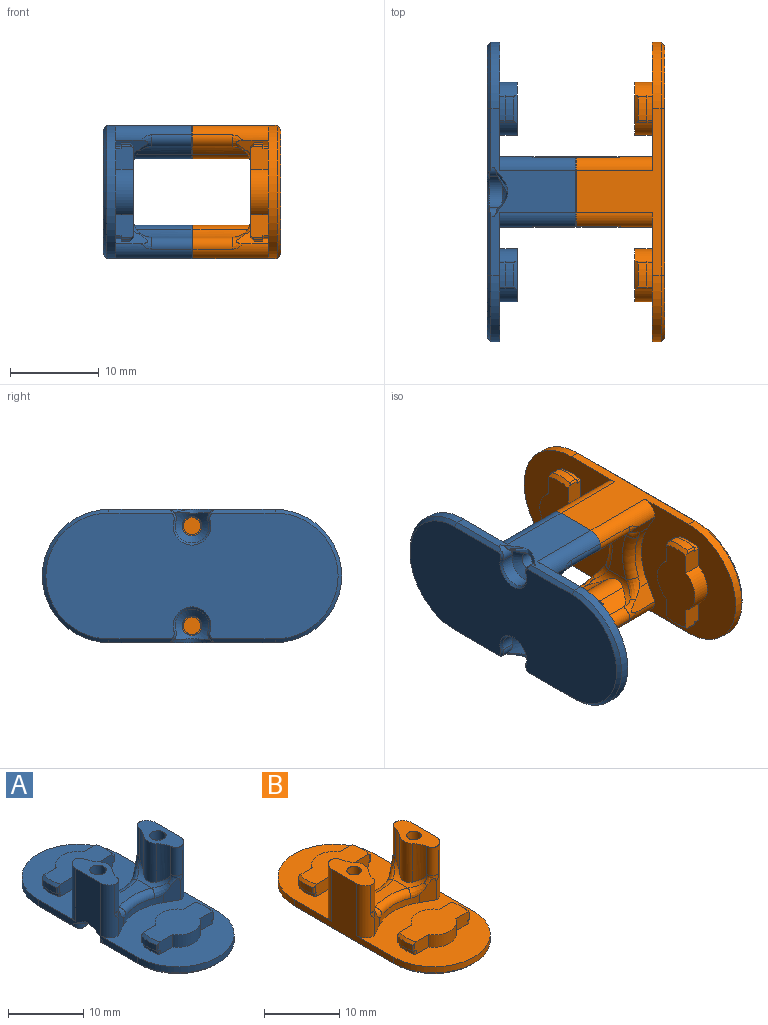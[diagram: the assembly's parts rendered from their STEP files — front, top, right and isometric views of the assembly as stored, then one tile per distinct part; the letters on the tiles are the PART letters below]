
ASSEMBLY  parts=2 mates=1
PART A: 116 faces, bbox 16.5x33.9x10.1 mm
  f0: plane 2.76x2mm, normal (0,-1,0), area 5mm2, adj f2,f13,f71,f76,f99,f105,f114
  f1: plane 2.57x2mm, normal (0,1,0), area 5mm2, adj f12,f78,f83,f87,f93,f101,f109
  f2: cylinder r=5.55mm len=2.91mm, axis (0,0,-1), area 2.9mm2, adj f0,f84,f99,f114,f115
  f3: cylinder r=5.55mm len=2.72mm, axis (0,0,-1), area 2.8mm2, adj f86,f95,f110,f111
  f4: cylinder r=7.55mm len=7.55mm, axis (0,0,1), area 8.2mm2, adj f11,f12,f38,f39,f88,f89
  f5: cylinder r=7.55mm len=7.55mm, axis (0,0,1), area 8.2mm2, adj f9,f13,f33,f34,f90,f91
  f6: cylinder r=1.6mm len=8.6mm, axis (0,0,1), area 19mm2, adj f10,f12,f26,f28,f37,f89
  f7: cylinder r=1.6mm len=8.6mm, axis (0,0,1), area 19mm2, adj f8,f13,f23,f24,f32,f91
  f8: bspline ~2.21x1.97mm, area 1.8mm2, adj f7,f9,f21,f32,f91
  f9: bspline ~2.95x2.65mm, area 2.9mm2, adj f5,f8,f21,f33,f91
  f10: bspline ~2.21x1.97mm, area 1.8mm2, adj f6,f11,f22,f37,f89
  f11: bspline ~2.95x2.65mm, area 2.9mm2, adj f4,f10,f22,f38,f89
  f12: plane 15.05x15mm, normal (0,0,1), area 143.6mm2, adj f1,f4,f6,f24,f26,f27,f30,f78
  f13: plane 15.05x15mm, normal (0,0,1), area 143.6mm2, adj f0,f5,f7,f24,f25,f26,f31,f70
  f14: plane 0.09x0mm, normal (0,0,-1), area 0mm2, adj f24,f59
  f15: plane 0.09x0mm, normal (0,0,-1), area 0mm2, adj f26,f57
  f16: plane 32.95x14.2mm, normal (0,0,-1), area 397.9mm2, adj f19,f20,f48,f49,f50,f51,f62,f63
  f17: cylinder r=1.1mm len=7.5mm, axis (0,0,1), area 51.8mm2, adj f23,f61
  f18: cylinder r=1.1mm len=7.5mm, axis (0,0,1), area 51.8mm2, adj f28,f60
  f19: plane 7.23x0.48mm, normal (0.71,0,-0.71), area 4mm2, adj f16,f24,f51,f58,f65
  f20: plane 7.23x0.48mm, normal (-0.71,0,-0.71), area 4mm2, adj f16,f26,f48,f57,f62
  f21: cylinder r=2mm len=5.89mm, axis (0,1,0), area 6.2mm2, adj f8,f9,f29,f39,f40,f42,f43,f44
  f22: cylinder r=2mm len=5.89mm, axis (0,-1,0), area 6.2mm2, adj f10,f11,f29,f34,f35,f45,f46,f47
  f23: plane 7.89x3.75mm, normal (0,0,1), area 18mm2, adj f7,f17,f24,f30,f32,f41,f42,f43
  f24: plane 18.89x9.74mm, normal (1,0,0), area 52.5mm2, adj f7,f12,f13,f14,f19,f23,f25,f27
  f25: cylinder r=7.5mm len=15mm, axis (0,0,-1), area 23.6mm2, adj f13,f24,f26,f51
  f26: plane 18.89x9.74mm, normal (-1,0,0), area 52.5mm2, adj f6,f12,f13,f15,f20,f25,f27,f28
  f27: cylinder r=7.5mm len=15mm, axis (0,0,-1), area 23.6mm2, adj f12,f24,f26,f48
  f28: plane 7.89x3.75mm, normal (0,0,1), area 18mm2, adj f6,f18,f26,f31,f36,f37,f45,f46
  f29: plane 6.2x2.81mm, normal (0,0,1), area 12.6mm2, adj f21,f22,f33,f38
  f30: cylinder r=1.6mm len=8.6mm, axis (0,0,1), area 19mm2, adj f12,f23,f24,f40,f41,f88
  f31: cylinder r=1.6mm len=8.6mm, axis (0,0,1), area 19mm2, adj f13,f26,f28,f35,f36,f90
  f32: cylinder r=1mm len=4.6mm, axis (0,0,1), area 8.8mm2, adj f7,f8,f23,f43
  f33: torus R=8.55mm, axis (0,0,1), area 9.2mm2, adj f5,f9,f29,f34
  f34: bspline ~2.95x2.65mm, area 2.9mm2, adj f5,f22,f33,f35,f90
  f35: bspline ~2.21x1.97mm, area 1.8mm2, adj f22,f31,f34,f36,f90
  f36: cylinder r=1mm len=4.6mm, axis (0,0,1), area 8.8mm2, adj f28,f31,f35,f46
  f37: cylinder r=1mm len=4.6mm, axis (0,0,1), area 8.8mm2, adj f6,f10,f28,f47
  f38: torus R=8.55mm, axis (0,0,1), area 9.2mm2, adj f4,f11,f29,f39
  f39: bspline ~2.95x2.65mm, area 2.9mm2, adj f4,f21,f38,f40,f88
  f40: bspline ~2.21x1.97mm, area 1.8mm2, adj f21,f30,f39,f41,f88
  f41: cylinder r=1mm len=4.6mm, axis (0,0,1), area 8.8mm2, adj f23,f30,f40,f44
  f42: cylinder r=1.88mm len=6.29mm, axis (0,0,1), area 16.2mm2, adj f21,f23,f43,f44
  f43: cylinder r=5mm len=6.29mm, axis (0,0,1), area 10.9mm2, adj f21,f23,f32,f42
  f44: cylinder r=5mm len=6.29mm, axis (0,0,1), area 10.9mm2, adj f21,f23,f41,f42
  f45: cylinder r=1.88mm len=6.29mm, axis (0,0,1), area 16.2mm2, adj f22,f28,f46,f47
  f46: cylinder r=5mm len=6.29mm, axis (0,0,1), area 10.9mm2, adj f22,f28,f36,f45
  f47: cylinder r=5mm len=6.29mm, axis (0,0,1), area 10.9mm2, adj f22,f28,f37,f45
  f48: cone r=7.5mm half-angle=45deg, axis (0,0,1), area 13mm2, adj f16,f20,f27,f49
  f49: plane 7.23x0.48mm, normal (0.71,0,-0.71), area 4mm2, adj f16,f24,f48,f59,f67
  f50: plane 7.23x0.48mm, normal (-0.71,0,-0.71), area 4mm2, adj f16,f26,f51,f56,f64
  f51: cone r=7.5mm half-angle=45deg, axis (0,0,1), area 13mm2, adj f16,f19,f25,f50
  f52: cylinder r=1.9mm len=3.8mm, axis (0,0,-1), area 10.4mm2, adj f56,f57,f60,f63
  f53: plane 0.09x0mm, normal (0,0,-1), area 0mm2, adj f26,f56
  f54: cylinder r=1.9mm len=3.8mm, axis (0,0,-1), area 10.4mm2, adj f58,f59,f61,f66
  f55: plane 0.09x0mm, normal (0,0,-1), area 0mm2, adj f24,f58
  f56: cylinder r=1mm len=1.46mm, axis (0,0,-1), area 1.8mm2, adj f26,f50,f52,f53,f60,f64,f69
  f57: cylinder r=1mm len=1.46mm, axis (0,0,-1), area 1.8mm2, adj f15,f20,f26,f52,f60,f62,f69
  f58: cylinder r=1mm len=1.46mm, axis (0,0,-1), area 1.8mm2, adj f19,f24,f54,f55,f61,f65,f68
  f59: cylinder r=1mm len=1.46mm, axis (0,0,-1), area 1.8mm2, adj f14,f24,f49,f54,f61,f67,f68
  f60: cone r=1.1mm half-angle=45deg, axis (0,0,-1), area 10.8mm2, adj f18,f52,f56,f57,f69
  f61: cone r=2.8mm half-angle=45deg, axis (0,0,-1), area 10.8mm2, adj f17,f54,f58,f59,f68
  f62: cone r=0.76mm half-angle=45deg, axis (0,0,1), area 0.4mm2, adj f16,f20,f57,f63
  f63: cone r=1.9mm half-angle=45deg, axis (0,0,-1), area 2.6mm2, adj f16,f52,f62,f64
  f64: cone r=0.76mm half-angle=45deg, axis (0,0,1), area 0.4mm2, adj f16,f50,f56,f63
  f65: cone r=0.76mm half-angle=45deg, axis (0,0,1), area 0.4mm2, adj f16,f19,f58,f66
  f66: cone r=1.9mm half-angle=45deg, axis (0,0,-1), area 2.6mm2, adj f16,f54,f65,f67
  f67: cone r=0.76mm half-angle=45deg, axis (0,0,1), area 0.4mm2, adj f16,f49,f59,f66
  f68: bspline ~5.35x1.67mm, area 2.3mm2, adj f24,f58,f59,f61
  f69: bspline ~5.83x1.88mm, area 2.3mm2, adj f26,f56,f57,f60
  f70: plane 2.57x2mm, normal (0,-1,0), area 5mm2, adj f13,f71,f76,f85,f97,f106,f113
  f71: cylinder r=3mm len=5.14mm, axis (0,0,-1), area 12.3mm2, adj f0,f13,f70,f76
  f72: plane 2.57x2mm, normal (0,1,0), area 5mm2, adj f13,f73,f76,f84,f99,f104,f115
  f73: cylinder r=3mm len=5.14mm, axis (0,0,-1), area 12.3mm2, adj f13,f72,f74,f76
  f74: plane 2.57x2mm, normal (0,1,0), area 5mm2, adj f13,f73,f76,f85,f97,f107,f112
  f75: cylinder r=5.55mm len=2.72mm, axis (0,0,-1), area 2.8mm2, adj f85,f97,f112,f113
  f76: plane 10.36x6.06mm, normal (0,0,1), area 42mm2, adj f0,f70,f71,f72,f73,f74,f84,f85
  f77: cylinder r=5.55mm len=2.72mm, axis (0,0,-1), area 2.8mm2, adj f87,f93,f108,f109
  f78: cylinder r=3mm len=5.14mm, axis (0,0,-1), area 12.3mm2, adj f1,f12,f79,f83
  f79: plane 2.57x2mm, normal (0,1,0), area 5mm2, adj f12,f78,f83,f86,f95,f103,f110
  f80: plane 2.57x2mm, normal (0,-1,0), area 5mm2, adj f12,f81,f83,f86,f95,f102,f111
  f81: cylinder r=3mm len=5.14mm, axis (0,0,-1), area 12.3mm2, adj f12,f80,f82,f83
  f82: plane 2.57x2mm, normal (0,-1,0), area 5mm2, adj f12,f81,f83,f87,f93,f100,f108
  f83: plane 10.3x6mm, normal (0,0,1), area 42mm2, adj f1,f78,f79,f80,f81,f82,f86,f87
  f84: cone r=5.15mm half-angle=45deg, axis (0,0,-1), area 1.6mm2, adj f2,f72,f76,f114,f115
  f85: cone r=5.15mm half-angle=45deg, axis (0,0,-1), area 1.7mm2, adj f70,f74,f75,f76,f112,f113
  f86: cone r=5.15mm half-angle=45deg, axis (0,0,-1), area 1.7mm2, adj f3,f79,f80,f83,f110,f111
  f87: cone r=5.15mm half-angle=45deg, axis (0,0,-1), area 1.7mm2, adj f1,f77,f82,f83,f108,f109
  f88: plane 3.63x2.12mm, normal (-0.48,-0.87,0), area 6.1mm2, adj f4,f12,f30,f39,f40
  f89: plane 3.63x2.12mm, normal (0.48,-0.87,0), area 6.1mm2, adj f4,f6,f10,f11,f12
  f90: plane 3.63x2.12mm, normal (0.48,0.87,0), area 6.1mm2, adj f5,f13,f31,f34,f35
  f91: plane 3.63x2.12mm, normal (-0.48,0.87,0), area 6.1mm2, adj f5,f7,f8,f9,f13
  f92: cylinder r=5.55mm len=2.72mm, axis (0,0,1), area 1.7mm2, adj f12,f93,f100,f101
  f93: plane 3.1x0.66mm, normal (0,0,-1), area 0.8mm2, adj f1,f77,f82,f92,f100,f101,f108,f109
  f94: cylinder r=5.55mm len=2.72mm, axis (0,0,1), area 1.7mm2, adj f12,f95,f102,f103
  f95: plane 3.1x0.66mm, normal (0,0,-1), area 0.8mm2, adj f3,f79,f80,f94,f102,f103,f110,f111
  f96: cylinder r=5.55mm len=2.72mm, axis (0,0,1), area 1.7mm2, adj f13,f97,f106,f107
  f97: plane 3.1x0.66mm, normal (0,0,-1), area 0.8mm2, adj f70,f74,f75,f96,f106,f107,f112,f113
  f98: cylinder r=5.55mm len=2.72mm, axis (0,0,1), area 1.7mm2, adj f13,f99,f104,f105
  f99: plane 3.1x0.66mm, normal (0,0,-1), area 0.8mm2, adj f0,f2,f72,f98,f104,f105,f115
  f100: cylinder r=0.25mm len=0.6mm, axis (0,0,1), area 0.2mm2, adj f12,f82,f92,f93
  f101: cylinder r=0.25mm len=0.6mm, axis (0,0,1), area 0.2mm2, adj f1,f12,f92,f93
  f102: cylinder r=0.25mm len=0.6mm, axis (0,0,1), area 0.2mm2, adj f12,f80,f94,f95
  f103: cylinder r=0.25mm len=0.6mm, axis (0,0,1), area 0.2mm2, adj f12,f79,f94,f95
  f104: cylinder r=0.25mm len=0.6mm, axis (0,0,1), area 0.2mm2, adj f13,f72,f98,f99
  f105: cylinder r=0.25mm len=0.6mm, axis (0,0,1), area 0.2mm2, adj f0,f13,f98,f99
  f106: cylinder r=0.25mm len=0.6mm, axis (0,0,1), area 0.2mm2, adj f13,f70,f96,f97
  f107: cylinder r=0.25mm len=0.6mm, axis (0,0,1), area 0.2mm2, adj f13,f74,f96,f97
  f108: cylinder r=0.25mm len=1.18mm, axis (0,0,-1), area 0.4mm2, adj f77,f82,f87,f93
  f109: cylinder r=0.25mm len=1.18mm, axis (0,0,-1), area 0.4mm2, adj f1,f77,f87,f93
  f110: cylinder r=0.25mm len=1.18mm, axis (0,0,-1), area 0.4mm2, adj f3,f79,f86,f95
  f111: cylinder r=0.25mm len=1.18mm, axis (0,0,-1), area 0.4mm2, adj f3,f80,f86,f95
  f112: cylinder r=0.25mm len=1.18mm, axis (0,0,-1), area 0.4mm2, adj f74,f75,f85,f97
  f113: cylinder r=0.25mm len=1.18mm, axis (0,0,-1), area 0.4mm2, adj f70,f75,f85,f97
  f114: bspline ~3.95x3.86mm, area 0.3mm2, adj f0,f2,f76,f84
  f115: cylinder r=0.25mm len=1.18mm, axis (0,0,-1), area 0.4mm2, adj f2,f72,f84,f99
PART B: 96 faces, bbox 15.1x33.8x10.1 mm
  f0: plane 2.57x2mm, normal (0,-1,0), area 5mm2, adj f12,f50,f56,f65,f77,f85,f93
  f1: plane 2.57x2mm, normal (0,1,0), area 5mm2, adj f24,f62,f63,f67,f75,f82,f88
  f2: cylinder r=5.55mm len=2.72mm, axis (0,0,-1), area 2.8mm2, adj f65,f77,f92,f93
  f3: cylinder r=5.55mm len=2.72mm, axis (0,0,-1), area 2.8mm2, adj f66,f73,f90,f91
  f4: cylinder r=7.55mm len=7.55mm, axis (0,0,1), area 8.2mm2, adj f11,f24,f34,f35,f68,f69
  f5: cylinder r=7.55mm len=7.55mm, axis (0,0,1), area 8.2mm2, adj f9,f12,f29,f30,f70,f71
  f6: cylinder r=1.6mm len=8.5mm, axis (0,0,1), area 18.8mm2, adj f10,f21,f23,f24,f33,f69
  f7: cylinder r=1.6mm len=8.6mm, axis (0,0,1), area 19mm2, adj f8,f12,f18,f19,f28,f71
  f8: bspline ~2.21x1.97mm, area 1.8mm2, adj f7,f9,f15,f28,f71
  f9: bspline ~2.95x2.65mm, area 2.9mm2, adj f5,f8,f15,f29,f71
  f10: bspline ~2.21x1.97mm, area 1.8mm2, adj f6,f11,f17,f33,f69
  f11: bspline ~2.53x2.49mm, area 2.9mm2, adj f4,f10,f17,f34,f69
  f12: plane 15.05x15mm, normal (0,0,1), area 143.6mm2, adj f0,f5,f7,f19,f20,f21,f27,f50
  f13: cylinder r=0.97mm len=7.9mm, axis (0,0,1), area 48.4mm2, adj f23,f45
  f14: cylinder r=0.97mm len=8mm, axis (0,0,1), area 49mm2, adj f18,f44
  f15: cylinder r=2mm len=5.89mm, axis (0,1,0), area 6.2mm2, adj f8,f9,f25,f35,f36,f38,f39,f40
  f16: plane 32.95x14.2mm, normal (0,0,-1), area 424.6mm2, adj f46,f47,f48,f49
  f17: cylinder r=2mm len=5.89mm, axis (0,-1,0), area 6.2mm2, adj f10,f11,f25,f30,f31,f41,f42,f43
  f18: plane 7.89x3.75mm, normal (0,0,1), area 18.8mm2, adj f7,f14,f19,f26,f28,f37,f38,f39
  f19: plane 18.75x9.6mm, normal (1,0,0), area 59.7mm2, adj f7,f12,f18,f20,f22,f24,f26,f47
  f20: cylinder r=7.5mm len=15mm, axis (0,0,-1), area 23.6mm2, adj f12,f19,f21,f49
  f21: plane 18.75x9.5mm, normal (-1,0,0), area 59.2mm2, adj f6,f12,f20,f22,f23,f24,f27,f48
  f22: cylinder r=7.5mm len=15mm, axis (0,0,-1), area 23.6mm2, adj f19,f21,f24,f46
  f23: plane 7.89x3.75mm, normal (0,0,1), area 18.8mm2, adj f6,f13,f21,f27,f32,f33,f41,f42
  f24: plane 15.05x15mm, normal (0,0,1), area 143.6mm2, adj f1,f4,f6,f19,f21,f22,f26,f58
  f25: plane 6.2x2.81mm, normal (0,0,1), area 12.6mm2, adj f15,f17,f29,f34
  f26: cylinder r=1.6mm len=8.6mm, axis (0,0,1), area 19mm2, adj f18,f19,f24,f36,f37,f68
  f27: cylinder r=1.6mm len=8.5mm, axis (0,0,1), area 18.8mm2, adj f12,f21,f23,f31,f32,f70
  f28: cylinder r=1mm len=4.6mm, axis (0,0,1), area 8.8mm2, adj f7,f8,f18,f39
  f29: torus R=8.55mm, axis (0,0,1), area 9.2mm2, adj f5,f9,f25,f30
  f30: bspline ~2.95x2.65mm, area 2.9mm2, adj f5,f17,f29,f31,f70
  f31: bspline ~2.21x1.97mm, area 1.8mm2, adj f17,f27,f30,f32,f70
  f32: cylinder r=1mm len=4.5mm, axis (0,0,1), area 8.6mm2, adj f23,f27,f31,f42
  f33: cylinder r=1mm len=4.5mm, axis (0,0,1), area 8.6mm2, adj f6,f10,f23,f43
  f34: torus R=8.55mm, axis (0,0,1), area 9.2mm2, adj f4,f11,f25,f35
  f35: bspline ~2.95x2.65mm, area 2.9mm2, adj f4,f15,f34,f36,f68
  f36: bspline ~2.21x1.97mm, area 1.8mm2, adj f15,f26,f35,f37,f68
  f37: cylinder r=1mm len=4.6mm, axis (0,0,1), area 8.8mm2, adj f18,f26,f36,f40
  f38: cylinder r=1.88mm len=6.29mm, axis (0,0,1), area 16.2mm2, adj f15,f18,f39,f40
  f39: cylinder r=5mm len=6.29mm, axis (0,0,1), area 10.9mm2, adj f15,f18,f28,f38
  f40: cylinder r=5mm len=6.29mm, axis (0,0,1), area 10.9mm2, adj f15,f18,f37,f38
  f41: cylinder r=1.88mm len=6.19mm, axis (0,0,1), area 15.9mm2, adj f17,f23,f42,f43
  f42: cylinder r=5mm len=6.19mm, axis (0,0,1), area 10.7mm2, adj f17,f23,f32,f41
  f43: cylinder r=5mm len=6.19mm, axis (0,0,1), area 10.7mm2, adj f17,f23,f33,f41
  f44: plane 1.95x1.95mm, normal (0,0,1), area 3mm2, adj f14
  f45: plane 1.95x1.95mm, normal (0,0,1), area 3mm2, adj f13
  f46: cone r=7.5mm half-angle=45deg, axis (0,0,1), area 13mm2, adj f16,f22,f47,f48
  f47: plane 18.75x0.4mm, normal (0.71,0,-0.71), area 10.6mm2, adj f16,f19,f46,f49
  f48: plane 18.75x0.4mm, normal (-0.71,0,-0.71), area 10.6mm2, adj f16,f21,f46,f49
  f49: cone r=7.5mm half-angle=45deg, axis (0,0,1), area 13mm2, adj f16,f20,f47,f48
  f50: cylinder r=3mm len=5.14mm, axis (0,0,-1), area 12.3mm2, adj f0,f12,f51,f56
  f51: plane 2.57x2mm, normal (0,-1,0), area 5mm2, adj f12,f50,f56,f64,f79,f87,f94
  f52: cylinder r=5.55mm len=2.72mm, axis (0,0,-1), area 2.8mm2, adj f64,f79,f94,f95
  f53: plane 2.57x2mm, normal (0,1,0), area 5mm2, adj f12,f54,f56,f64,f79,f86,f95
  f54: cylinder r=3mm len=5.14mm, axis (0,0,-1), area 12.3mm2, adj f12,f53,f55,f56
  f55: plane 2.57x2mm, normal (0,1,0), area 5mm2, adj f12,f54,f56,f65,f77,f84,f92
  f56: plane 10.3x6mm, normal (0,0,1), area 42mm2, adj f0,f50,f51,f53,f54,f55,f64,f65
  f57: cylinder r=5.55mm len=2.72mm, axis (0,0,-1), area 2.8mm2, adj f67,f75,f88,f89
  f58: plane 2.57x2mm, normal (0,-1,0), area 5mm2, adj f24,f59,f63,f67,f75,f83,f89
  f59: cylinder r=3mm len=5.14mm, axis (0,0,-1), area 12.3mm2, adj f24,f58,f60,f63
  f60: plane 2.57x2mm, normal (0,-1,0), area 5mm2, adj f24,f59,f63,f66,f73,f81,f90
  f61: plane 2.57x2mm, normal (0,1,0), area 5mm2, adj f24,f62,f63,f66,f73,f80,f91
  f62: cylinder r=3mm len=5.14mm, axis (0,0,-1), area 12.3mm2, adj f1,f24,f61,f63
  f63: plane 10.3x6mm, normal (0,0,1), area 42mm2, adj f1,f58,f59,f60,f61,f62,f66,f67
  f64: cone r=5.55mm half-angle=45deg, axis (0,0,-1), area 1.7mm2, adj f51,f52,f53,f56,f94,f95
  f65: cone r=5.55mm half-angle=45deg, axis (0,0,-1), area 1.7mm2, adj f0,f2,f55,f56,f92,f93
  f66: cone r=5.55mm half-angle=45deg, axis (0,0,-1), area 1.7mm2, adj f3,f60,f61,f63,f90,f91
  f67: cone r=5.55mm half-angle=45deg, axis (0,0,-1), area 1.7mm2, adj f1,f57,f58,f63,f88,f89
  f68: plane 3.63x2.12mm, normal (-0.48,-0.87,0), area 6.1mm2, adj f4,f24,f26,f35,f36
  f69: plane 3.63x2.12mm, normal (0.48,-0.87,0), area 6.1mm2, adj f4,f6,f10,f11,f24
  f70: plane 3.63x2.12mm, normal (0.48,0.87,0), area 6.1mm2, adj f5,f12,f27,f30,f31
  f71: plane 3.63x2.12mm, normal (-0.48,0.87,0), area 6.1mm2, adj f5,f7,f8,f9,f12
  f72: cylinder r=5.55mm len=2.72mm, axis (0,0,1), area 1.7mm2, adj f24,f73,f80,f81
  f73: plane 3.1x0.66mm, normal (0,0,-1), area 0.8mm2, adj f3,f60,f61,f72,f80,f81,f90,f91
  f74: cylinder r=5.55mm len=2.72mm, axis (0,0,1), area 1.7mm2, adj f24,f75,f82,f83
  f75: plane 3.1x0.66mm, normal (0,0,-1), area 0.8mm2, adj f1,f57,f58,f74,f82,f83,f88,f89
  f76: cylinder r=5.55mm len=2.72mm, axis (0,0,1), area 1.7mm2, adj f12,f77,f84,f85
  f77: plane 3.1x0.66mm, normal (0,0,-1), area 0.8mm2, adj f0,f2,f55,f76,f84,f85,f92,f93
  f78: cylinder r=5.55mm len=2.72mm, axis (0,0,1), area 1.7mm2, adj f12,f79,f86,f87
  f79: plane 3.1x0.66mm, normal (0,0,-1), area 0.8mm2, adj f51,f52,f53,f78,f86,f87,f94,f95
  f80: cylinder r=0.25mm len=0.6mm, axis (0,0,1), area 0.2mm2, adj f24,f61,f72,f73
  f81: cylinder r=0.25mm len=0.6mm, axis (0,0,1), area 0.2mm2, adj f24,f60,f72,f73
  f82: cylinder r=0.25mm len=0.6mm, axis (0,0,1), area 0.2mm2, adj f1,f24,f74,f75
  f83: cylinder r=0.25mm len=0.6mm, axis (0,0,1), area 0.2mm2, adj f24,f58,f74,f75
  f84: cylinder r=0.25mm len=0.6mm, axis (0,0,1), area 0.2mm2, adj f12,f55,f76,f77
  f85: cylinder r=0.25mm len=0.6mm, axis (0,0,1), area 0.2mm2, adj f0,f12,f76,f77
  f86: cylinder r=0.25mm len=0.6mm, axis (0,0,1), area 0.2mm2, adj f12,f53,f78,f79
  f87: cylinder r=0.25mm len=0.6mm, axis (0,0,1), area 0.2mm2, adj f12,f51,f78,f79
  f88: cylinder r=0.25mm len=1.18mm, axis (0,0,-1), area 0.4mm2, adj f1,f57,f67,f75
  f89: cylinder r=0.25mm len=1.18mm, axis (0,0,-1), area 0.4mm2, adj f57,f58,f67,f75
  f90: cylinder r=0.25mm len=1.18mm, axis (0,0,-1), area 0.4mm2, adj f3,f60,f66,f73
  f91: cylinder r=0.25mm len=1.18mm, axis (0,0,-1), area 0.4mm2, adj f3,f61,f66,f73
  f92: cylinder r=0.25mm len=1.18mm, axis (0,0,-1), area 0.4mm2, adj f2,f55,f65,f77
  f93: cylinder r=0.25mm len=1.18mm, axis (0,0,-1), area 0.4mm2, adj f0,f2,f65,f77
  f94: cylinder r=0.25mm len=1.18mm, axis (0,0,-1), area 0.4mm2, adj f51,f52,f64,f79
  f95: cylinder r=0.25mm len=1.18mm, axis (0,0,-1), area 0.4mm2, adj f52,f53,f64,f79
PLACE A rot(axis=(0,1,0),90deg) t=(-5.17,2.75,-4.57)mm
PLACE B rot(axis=(0,-1,0),90deg) t=(14.83,2.75,-21.57)mm
MATE fastened A.f18 <-> B.f14  axis (1,0,0) through (4.83,2.75,1.05)mm
